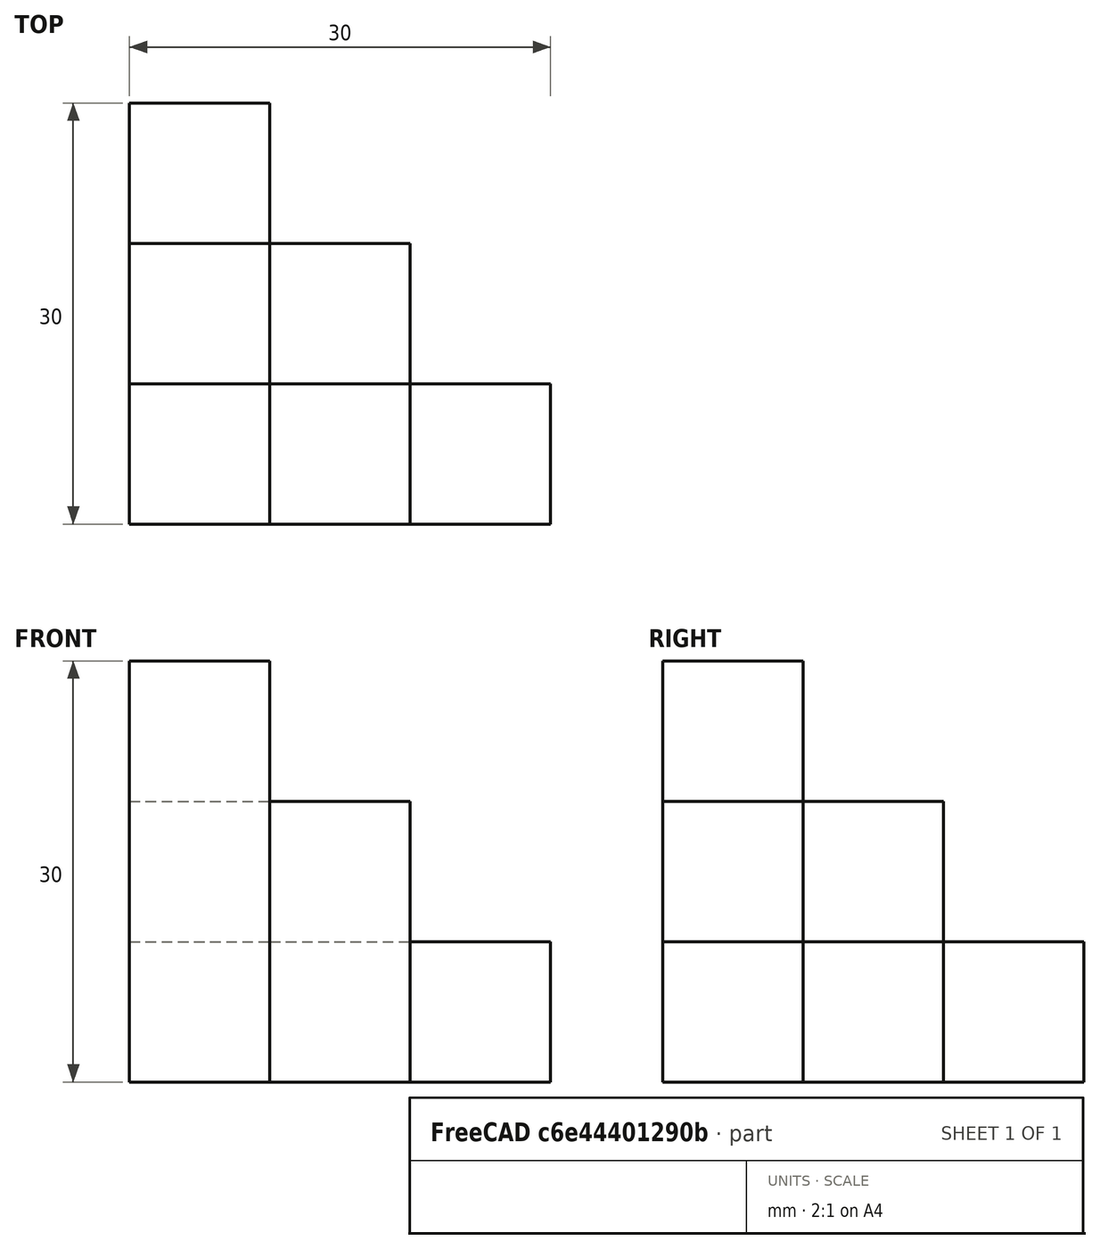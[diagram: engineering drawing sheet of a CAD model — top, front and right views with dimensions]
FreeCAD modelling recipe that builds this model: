
FCSTD DOCUMENT  (FreeCAD 1.0R39319 (Git))
Label: ojt_t04r01_qbert 3 levels
License: All rights reserved
LicenseURL: https://en.wikipedia.org/wiki/All_rights_reserved
objects: Part::Box×6, PartDesign::Body×1
note: 7 computed .brp shape members not serialized (recipe doc carries the construction recipe); baked Part::Feature solids carry a one-line shape summary decoded from their .brp

FEATURE [PartDesign::Body] Body  label="Cuerpo"
  AllowCompound = false
  Origin = -> Origin
FEATURE [Part::Box] Box  label="Cubo"
  AttacherType = Attacher::AttachEngine3D
  Height = 30
  Length = 10
  Width = 10
FEATURE [Part::Box] Box001  label="Cubo001"
  AttacherType = Attacher::AttachEngine3D
  Height = 20
  Length = 10
  Placement = pos=(0,10,0) rot=(0,0,1;0rad)
  Width = 10
FEATURE [Part::Box] Box002  label="Cubo002"
  AttacherType = Attacher::AttachEngine3D
  Height = 20
  Length = 10
  Placement = pos=(10,0,0) rot=(0,0,1;0rad)
  Width = 10
FEATURE [Part::Box] Box004  label="Cubo004"
  AttacherType = Attacher::AttachEngine3D
  Height = 10
  Length = 10
  Placement = pos=(10,10,0) rot=(0,0,1;0rad)
  Width = 10
FEATURE [Part::Box] Box005  label="Cubo005"
  AttacherType = Attacher::AttachEngine3D
  Height = 10
  Length = 10
  Placement = pos=(20,0,0) rot=(0,0,1;0rad)
  Width = 10
FEATURE [Part::Box] Box006  label="Cubo006"
  AttacherType = Attacher::AttachEngine3D
  Height = 10
  Length = 10
  Placement = pos=(0,20,0) rot=(0,0,1;0rad)
  Width = 10
